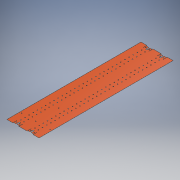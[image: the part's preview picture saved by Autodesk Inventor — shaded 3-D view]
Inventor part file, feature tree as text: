
AUTODESK INVENTOR PART (.ipt)
format: ipt  version: 2019 (Build 230136000, 136)  size: 447,488 bytes
history: native  units: mm
features: mirror x5, extrude x4, other x4
ambient origin geometry x8: Origin, YZ Plane, XZ Plane, XY Plane, X Axis, Y Axis, Z Axis, Center Point
bodies: Solid1 (feature_tree)
feature tree (13):
  extrude  "Skin Body"  Depth=2049.0mm
  extrude  "Feature Cut"  Depth=1024.5mm
  mirror  "Feature Cut Side Mirror"
  mirror  "Feature Cut Mirror"
  extrude  "End Cut"  Depth=424.0mm
  mirror  "End Cut Mirror"
  extrude  "Slot Cut"  Depth=212.0mm
  mirror  "Slot Cut Side Mirror"
  mirror  "Slot Cut Mirror"
  other  "Skin Scheme"
  other  "Feature Cut Outline"
  other  "End Cut Outline"
  other  "Slot Cut Outline"
